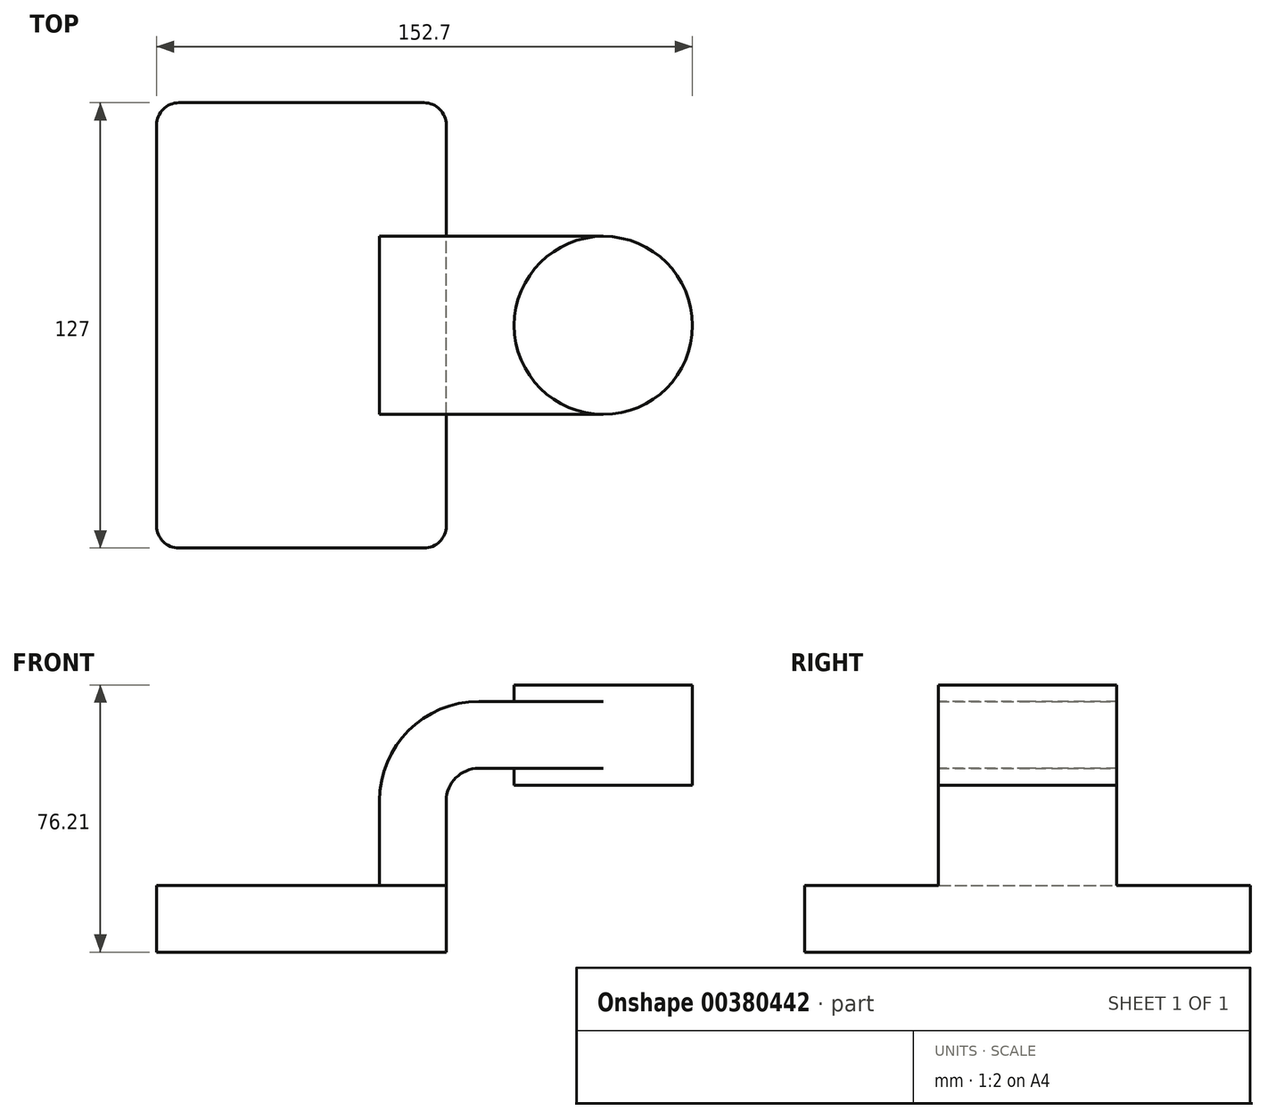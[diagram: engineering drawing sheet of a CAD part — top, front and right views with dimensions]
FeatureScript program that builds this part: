
annotation { "Feature Type Name" : "Feature", "Feature Type Description" : "" }
export const myFeature = defineFeature(function(context is Context, id is Id, definition is map)
    precondition{}
    {
        {
            var Q0;
            Q0=qCreatedBy(makeId("Front.planeOp"),FACE);
            var sketch = newSketch(context, id + "F0", { "sketchPlane" : qUnion([Q0])});
            skLineSegment(sketch, "E0.bottom", {"start": v(41.28, -9.52) * mm, "end": v(-41.28, -9.53) * mm});
            skLineSegment(sketch, "E0.top", {"start": v(41.28, 9.53) * mm, "end": v(-41.28, 9.53) * mm});
            skLineSegment(sketch, "E0.left", {"start": v(41.28, -9.52) * mm, "end": v(41.28, 9.53) * mm});
            skLineSegment(sketch, "E0.right", {"start": v(-41.28, -9.53) * mm, "end": v(-41.28, 9.53) * mm});
            skPoint(sketch, "E0.middle", {"position": v(0, 0) * mm});
            skLineSegment(sketch, "E1.bottom", {"start": v(111.43, 38.1) * mm, "end": v(60.63, 38.1) * mm});
            skLineSegment(sketch, "E1.top", {"start": v(111.43, 66.68) * mm, "end": v(60.63, 66.68) * mm});
            skLineSegment(sketch, "E1.left", {"start": v(111.43, 38.1) * mm, "end": v(111.43, 66.68) * mm});
            skLineSegment(sketch, "E1.right", {"start": v(60.63, 38.1) * mm, "end": v(60.63, 66.68) * mm});
            skPoint(sketch, "E1.middle", {"position": v(86.03, 52.39) * mm});
            skLineSegment(sketch, "E2", {"start": v(41.28, 9.53) * mm, "end": v(41.28, 33.62) * mm});
            skArc(sketch, "E3", {"start": v(41.28, 33.62) * mm, "mid": v(43.99, 40.16) * mm, "end": v(50.53, 42.88) * mm});
            skLineSegment(sketch, "E4", {"start": v(50.53, 42.88) * mm, "end": v(86.03, 42.88) * mm});
            skPoint(sketch, "E4.endSnap0", {"position": v(86.03, 38.1) * mm});
            skLineSegment(sketch, "E5.0", {"start": v(50.53, 61.93) * mm, "end": v(86.03, 61.93) * mm});
            skArc(sketch, "E5.1", {"start": v(22.23, 33.62) * mm, "mid": v(30.52, 53.63) * mm, "end": v(50.53, 61.93) * mm});
            skLineSegment(sketch, "E5.2", {"start": v(22.22, 9.53) * mm, "end": v(22.22, 33.62) * mm});
            skLineSegment(sketch, "E6", {"start": v(86.03, 38.1) * mm, "end": v(86.03, 61.93) * mm});
            skLineSegment(sketch, "E7", {"start": v(86.03, 61.93) * mm, "end": v(86.03, 66.68) * mm});
            skFitSpline(sketch, "E8", {"points": [v(-41.28, 9.53) * mm, v(50.53, 61.93) * mm], "startDerivative": vector(0.17, 68.37) * mm, "endDerivative": vector(151.6, -11.95) * mm});
            skSolve(sketch);
        }
        {
            var Q0;
            Q0=makeQuery(id+"F0.imprint","IMPRINT",FACE,{"disambiguationData":[TD([[makeQuery(id+"F0.imprint","IMPRINT",EDGE,{"derivedFrom":sQuery(id+"F0.wireOp",EDGE,"E0.bottom")}),-1.0]])]});
            extrude(context, id + "F1", {"entities" : qUnion([Q0]), "endBound" : BoundingType.SYMMETRIC, "depth" : 127 * mm});
        }
        {
            var Q0;
            {var subQ1=sQuery(id+"F0.wireOp",EDGE,"E2");Q0=makeQuery(id+"F0.imprint","IMPRINT",FACE,{"disambiguationData":[TD([[makeQuery(id+"F0.imprint","IMPRINT",EDGE,{"derivedFrom":subQ1}),1.0]])]});}
            var Q1;
            {var subQ0=sQuery(id+"F0.wireOp",EDGE,"E4");var subQ1=sQuery(id+"F0.wireOp",EDGE,"E1.right");var subQ2=makeQuery(id+"F0.imprint","INTERSECT",VERTEX,{"derivedFrom":[subQ1,subQ0]});Q1=makeQuery(id+"F0.imprint","IMPRINT",FACE,{"disambiguationData":[TD([[makeQuery(id+"F0.imprint","IMPRINT",EDGE,{"disambiguationData":[TD([[subQ2,-1.0]])],"derivedFrom":subQ1}),-1.0]])]});}
            extrude(context, id + "F2", {"entities" : qUnion([Q0, Q1]), "operationType" : NewBodyOperationType.ADD, "endBound" : BoundingType.SYMMETRIC, "depth" : 50.8 * mm});
        }
        {
            var Q0;
            Q0=makeQuery(id+"F0.imprint","IMPRINT",FACE,{"disambiguationData":[TD([[makeQuery(id+"F0.imprint","IMPRINT",EDGE,{"derivedFrom":sQuery(id+"F0.wireOp",EDGE,"E5.1")}),1.0]])]});
            extrude(context, id + "F3", {"entities" : qUnion([Q0]), "operationType" : NewBodyOperationType.ADD, "depth" : 15.88 * mm});
        }
        {
            var Q0;
            {var subQ4=sQuery(id+"F0.wireOp",EDGE,"E1.left");Q0=makeQuery(id+"F0.imprint","IMPRINT",FACE,{"disambiguationData":[TD([[makeQuery(id+"F0.imprint","IMPRINT",EDGE,{"derivedFrom":subQ4}),1.0]])]});}
            var Q1;
            Q1=sQuery(id+"F0.wireOp",EDGE,"E6");
            revolve(context, id + "F4", {"operationType" : NewBodyOperationType.ADD, "entities" : qUnion([Q0]), "axis" : qUnion([Q1]), "revolveType" : RevolveType.FULL});
        }
        {
            var Q0;
            Q0=makeQuery(id+"F1.opExtrude","CAP_EDGE",EDGE,{"disambiguationData":[OSD([sQuery(id+"F0.wireOp",EDGE,"E0.right")])],"isStart":false});
            var Q1;
            Q1=makeQuery(id+"F1.opExtrude","CAP_EDGE",EDGE,{"disambiguationData":[OSD([sQuery(id+"F0.wireOp",EDGE,"E0.left")])],"isStart":false});
            var Q2;
            Q2=makeQuery(id+"F1.opExtrude","CAP_EDGE",EDGE,{"disambiguationData":[OSD([sQuery(id+"F0.wireOp",EDGE,"E0.left")])],"isStart":true});
            var Q3;
            Q3=makeQuery(id+"F1.opExtrude","CAP_EDGE",EDGE,{"disambiguationData":[OSD([sQuery(id+"F0.wireOp",EDGE,"E0.right")])],"isStart":true});
            fillet(context, id + "F5", {"entities" : qUnion([Q0, Q1, Q2, Q3]), "radius" : 6.35 * mm, "tangentPropagation" : true, "allowEdgeOverflow" : false});
        }
    });
